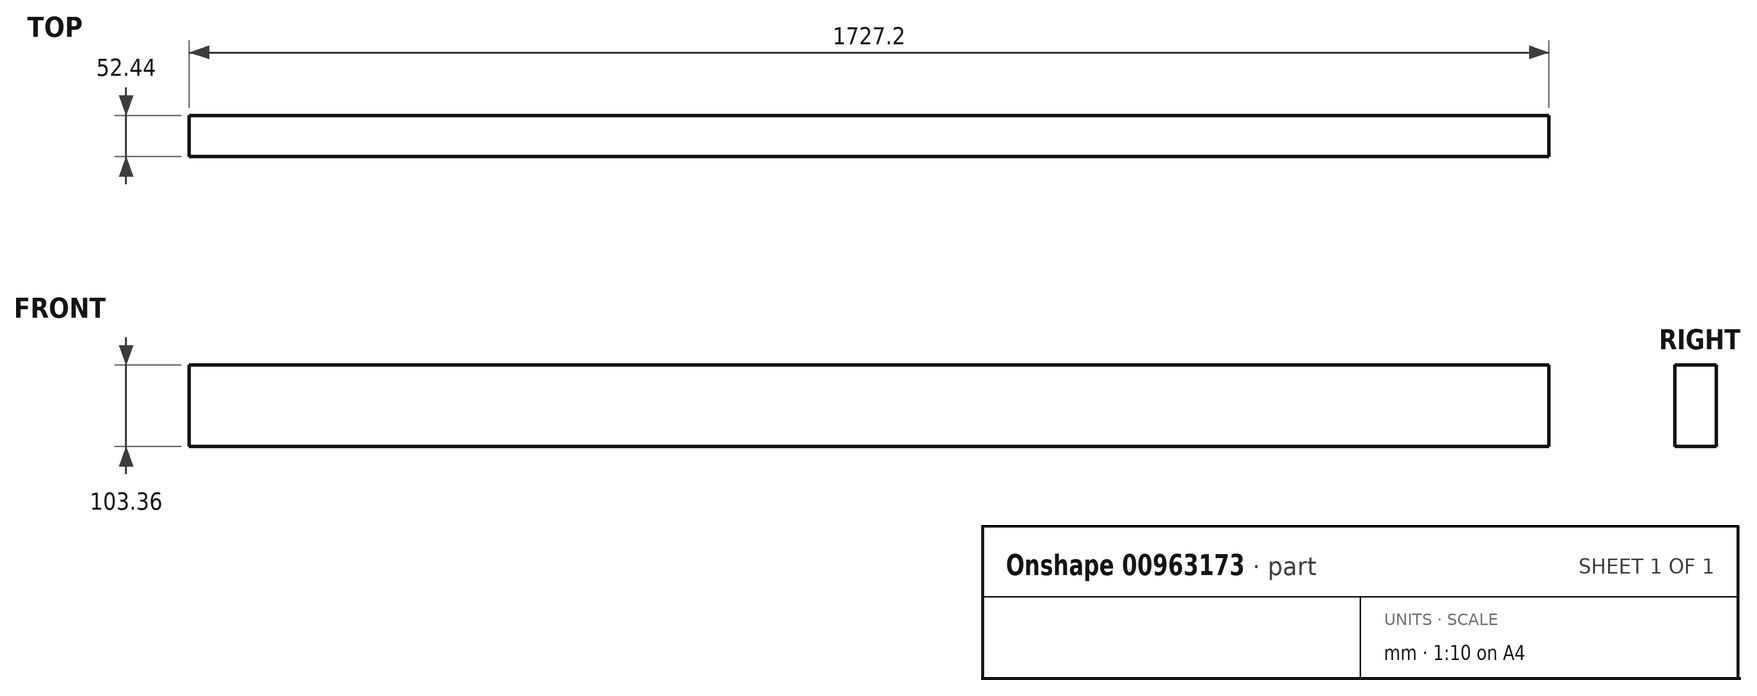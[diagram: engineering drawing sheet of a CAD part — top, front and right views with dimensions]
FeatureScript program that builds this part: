
annotation { "Feature Type Name" : "Feature", "Feature Type Description" : "" }
export const myFeature = defineFeature(function(context is Context, id is Id, definition is map)
    precondition{}
    {
        {
            var Q0;
            Q0=qCreatedBy(makeId("Right.planeOp"),FACE);
            var sketch = newSketch(context, id + "F0", { "sketchPlane" : qUnion([Q0])});
            skLineSegment(sketch, "E0.bottom", {"start": v(-26.22, 51.68) * mm, "end": v(26.22, 51.68) * mm});
            skLineSegment(sketch, "E0.top", {"start": v(-26.22, -51.68) * mm, "end": v(26.22, -51.68) * mm});
            skLineSegment(sketch, "E0.left", {"start": v(-26.22, 51.68) * mm, "end": v(-26.22, -51.68) * mm});
            skLineSegment(sketch, "E0.right", {"start": v(26.22, 51.68) * mm, "end": v(26.22, -51.68) * mm});
            skPoint(sketch, "E0.middle", {"position": v(0, 0) * mm});
            skSolve(sketch);
        }
        {
            var Q0;
            Q0=makeQuery(id+"F0.imprint","IMPRINT",FACE,{"disambiguationData":[TD([[makeQuery(id+"F0.imprint","IMPRINT",EDGE,{"derivedFrom":sQuery(id+"F0.wireOp",EDGE,"E0.bottom")}),-1.0]])]});
            extrude(context, id + "F1", {"entities" : qUnion([Q0]), "depth" : 1727.2 * mm, "offsetDistance" : 25.4 * mm});
        }
    });
